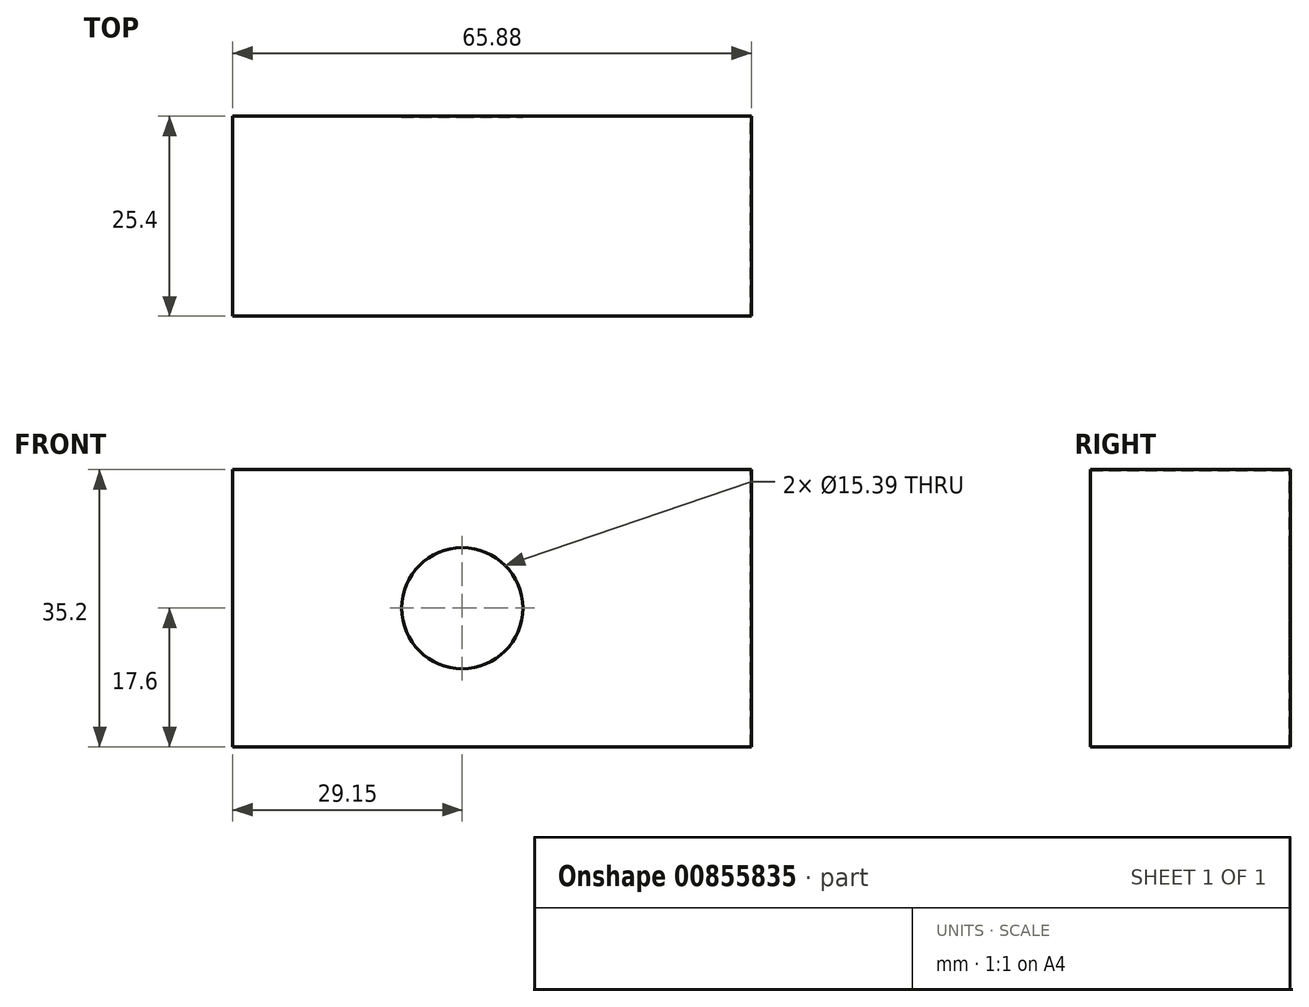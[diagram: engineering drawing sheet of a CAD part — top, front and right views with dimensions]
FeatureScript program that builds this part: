
annotation { "Feature Type Name" : "Feature", "Feature Type Description" : "" }
export const myFeature = defineFeature(function(context is Context, id is Id, definition is map)
    precondition{}
    {
        {
            var Q0;
            Q0=qCreatedBy(makeId("Front.planeOp"),FACE);
            var sketch = newSketch(context, id + "F0", { "sketchPlane" : qUnion([Q0])});
            skLineSegment(sketch, "E0.bottom", {"start": v(32.94, -17.6) * mm, "end": v(-32.94, -17.6) * mm});
            skLineSegment(sketch, "E0.top", {"start": v(32.94, 17.6) * mm, "end": v(-32.94, 17.6) * mm});
            skLineSegment(sketch, "E0.left", {"start": v(32.94, -17.6) * mm, "end": v(32.94, 17.6) * mm});
            skLineSegment(sketch, "E0.right", {"start": v(-32.94, -17.6) * mm, "end": v(-32.94, 17.6) * mm});
            skPoint(sketch, "E0.middle", {"position": v(0, 0) * mm});
            skSolve(sketch);
        }
        {
            var Q0;
            Q0 = qSketchRegion(id + "F0", true);
            extrude(context, id + "F1", {"entities" : qUnion([Q0]), "depth" : 25.4 * mm, "offsetDistance" : 25.4 * mm});
        }
        {
            var Q0;
            Q0=makeQuery(id+"F1.opExtrude","SWEPT_FACE",FACE,{"disambiguationData":[OSD([sQuery(id+"F0.wireOp",EDGE,"E0.bottom")])]});
            shell(context, id + "F2", {"entities" : qUnion([Q0]), "thickness" : 0.1 * mm});
        }
        {
            var Q0;
            Q0=makeQuery(id+"F1.opExtrude","CAP_FACE",FACE,{"disambiguationData":[OSD([sQuery(id+"F0.wireOp",EDGE,"E0.bottom"),sQuery(id+"F0.wireOp",EDGE,"E0.top"),sQuery(id+"F0.wireOp",EDGE,"E0.left"),sQuery(id+"F0.wireOp",EDGE,"E0.right")])],"isStart":false});
            var sketch = newSketch(context, id + "F3", { "sketchPlane" : qUnion([Q0])});
            skCircle(sketch, "E1", {"center": v(-3.79, 0) * mm, "radius": 7.7 * mm});
            skSolve(sketch);
        }
        {
            var Q0;
            Q0=makeQuery(id+"F3.imprint","IMPRINT",FACE,{"disambiguationData":[TD([[makeQuery(id+"F3.imprint","IMPRINT",EDGE,{"derivedFrom":sQuery(id+"F3.wireOp",EDGE,"E1")}),1.0]])]});
            extrude(context, id + "F4", {"entities" : qUnion([Q0]), "operationType" : NewBodyOperationType.REMOVE, "oppositeDirection" : true, "depth" : 42.93 * mm, "offsetDistance" : 25.4 * mm});
        }
    });
